# Revit family: Faucet-Wall_Mount-Lavatory-KALLISTA-Script-P25011_1
name_source: partatom
category: Plumbing Fixtures
units: mm (PartAtom-declared; Revit-internal decimal feet)

## family parameters
Cut with Voids When Loaded = No
Host = Face
OmniClass Number = 23.31.11.00
OmniClass Title = Faucets
Part Type = Normal
Room Calculation Point = No
Round Connector Dimension = Use Diameter
Shared = No

## types (6) — shared parameters
ADA Compliant = Yes
Assembly Code = D2010
CW Connection = Yes
Cold Water Inlet = Cold Water Inlet
Date Modified = 10/29/2022
Default Elevation = 36"
Description = WALL-MOUNT SINK FAUCET, LEVER HANDLES
Drain Included = Yes
Flow Rate = 1 GPM
HW Connection = Yes
Handle Clearance = 2 15/16"
Height = 2 5/16"
Hot Water Inlet = Hot Water Inlet
Length = 6 5/16"
Manufacturer = Kallista Co.
Master Format 2014 = 22 41 39
Master Format 2014 Name = Residential Faucets, Supplies, and Trim
Material = Solid Metal Construction
Pressure = 60.00 psi
Product Documentation Link = https://resources.kohler.com
Product Name = Script
Spout Reach = 6 5/16"
URL = https://www.kallista.com
Vent Connection = No
Waste Connection = No
Waste Water Outlet = Waste Water Outlet
WaterSense Certified = Yes

## per-type parameters (varying)
| type | Finish | Model | Product Page URL | Type |
| AD-Nickel Silver | Kallista-Metal-AD-Nickel_Silver | K-P25011-LV-AD | https://www.kallista.com | 1 |
| BAF-Brushed French Gold | Kallista-Metal-BAF-Brushed_French_Gold | K-P25011-LV-BAF | https://www.kallista.com | 2 |
| BV-Brushed Bronze | Kallista-Metal-BV-Brushed_Bronze | K-P25011-LV-BV | https://www.kallista.com | 4 |
| CP-Chrome | Kallista-Metal-CP-Chrome | K-P25011-LV-CP | https://www.kallista.com | 5 |
| SN-Polished Nickel | Kallista-Metal-SN-Polished_Nickel | K-P25011-LV-SN | https://www.kallista.com | 6 |
| BN-Brushed Nickel | Kallista-Metal-BN-Brushed_Nickel | K-P25011-LV-BN |  | 3 |

## geometry (parser evidence)
native form markers: Sweep x6
no freeform markers — native parametric forms only
